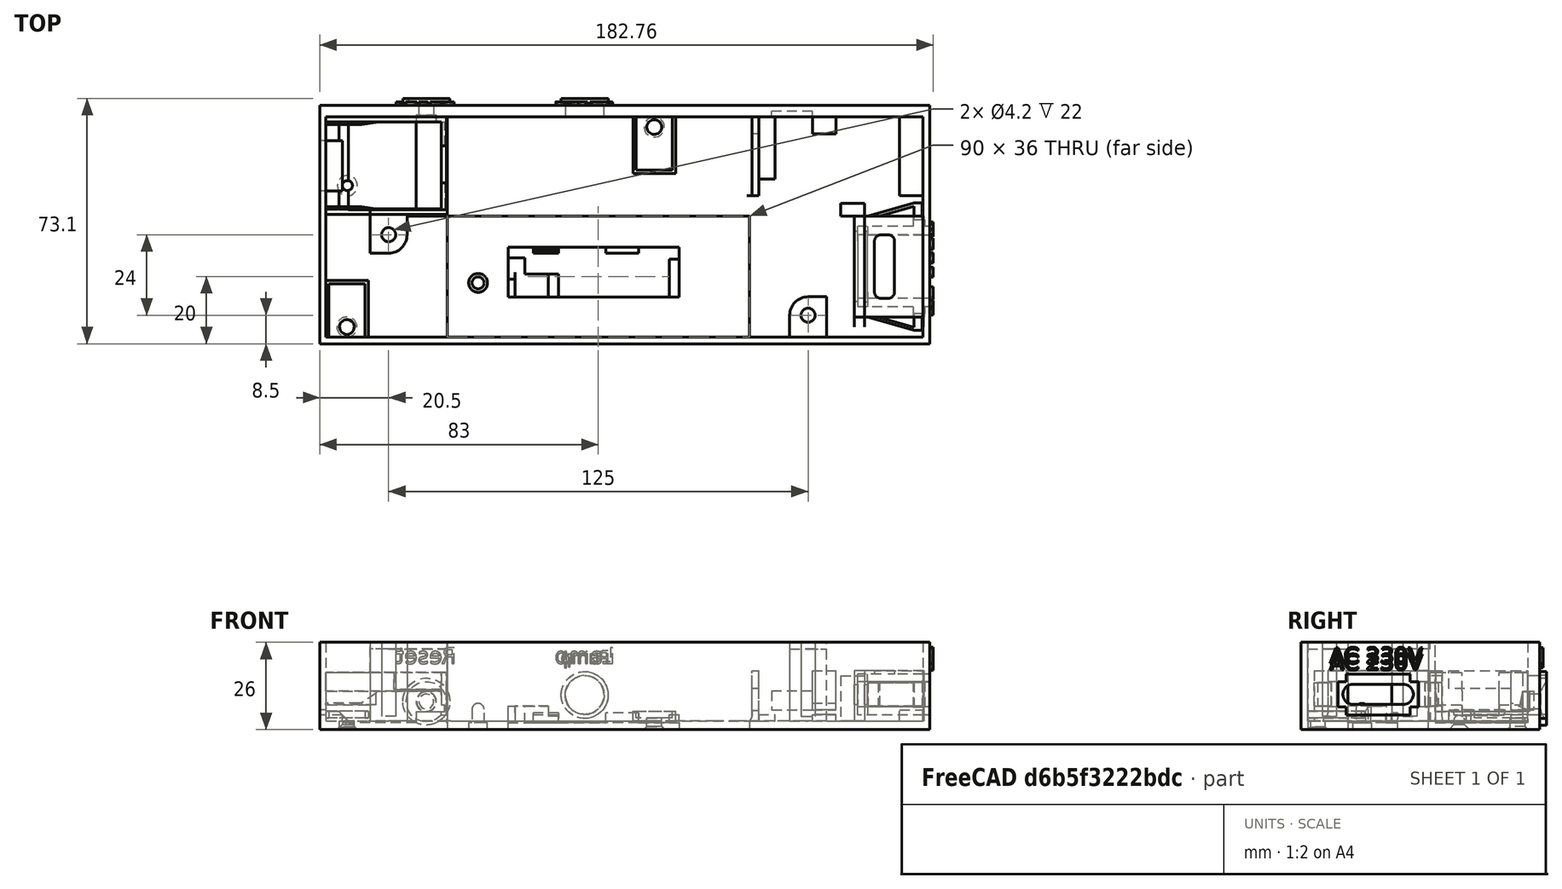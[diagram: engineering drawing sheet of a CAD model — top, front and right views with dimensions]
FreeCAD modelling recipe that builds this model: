
FCSTD DOCUMENT  (FreeCAD 0.21R33771 (Git))
Label: station.lamp.1x42V
License: All rights reserved
LicenseURL: http://en.wikipedia.org/wiki/All_rights_reserved
objects: Part::FeaturePython×10, Part::Extrusion×8, Part::Cut×6, Part::Feature×6, Part::MultiFuse×6, Part::Part2DObjectPython×6, App::DocumentObjectGroup×2, Part::Cone×1, Part::Refine×1
note: 44 computed .brp shape members not serialized (recipe doc carries the construction recipe); baked Part::Feature solids carry a one-line shape summary decoded from their .brp

FEATURE [Part::Cut] Cut008
FEATURE [Part::Feature] Cut008_solid  label="Cut008 (Solid)"
  shape: bbox 182.8 x 74.77 x 26 mm, 631 faces (baked)
FEATURE [Part::Feature] Fusion005002002014004003003002009002010004002003006003008008004007002004008002005001  label="Fusion005002002014004003003002009002010004002003006003008008004007002004008002006"
  Placement = pos=(-44.5951,-46.9627,187.501) rot=(0,0,1;1.5708rad)
  shape: bbox 50.9 x 14.8 x 7 mm, 30 faces (baked)
FEATURE [Part::MultiFuse] Fusion005002002014004003003002009002010004002003006003008008004007002004008002003
  Placement = pos=(333.004,-68.3059,2.13395) rot=(0,0,1;0rad)
FEATURE [Part::Part2DObjectPython] Rectangle  # Draft 2D object (typed FeaturePython)
  Area = 4964
  ChamferSize = 0
  Columns = 1
  FilletRadius = 0
  Height = 136
  Length = 36.5
  MakeFace = true
  Placement = pos=(136,3,22) rot=(0,0,1;1.5708rad)
  Rows = 1
FEATURE [Part::Extrusion] Extrusion
  Base = -> Rectangle
  Dir = (-8.1519e-11,-1.28811e-08,-2)
  DirMode = 0
  FaceMakerClass = Part::FaceMakerBullseye
  LengthFwd = 0
  LengthRev = 0
  Solid = true
  Symmetric = false
FEATURE [Part::Cut] Cut
  Base = -> Cut008_solid
  Tool = -> Extrusion
FEATURE [Part::Part2DObjectPython] Rectangle001  # Draft 2D object (typed FeaturePython)
  Area = 5003.74
  ChamferSize = 0
  Columns = 1
  FilletRadius = 0
  Height = 49.6839
  Length = 100.711
  MakeFace = true
  Placement = pos=(166.761,-20.8491,-24.6542) rot=(0.57735,0.57735,0.57735;2.0944rad)
  Rows = 1
FEATURE [Part::FeaturePython] Slice  # WARN: FeaturePython — macro-defined, semantics opaque (R4)
  Base = -> Cut
  Mode = 1
  Tolerance = 0
  Tools = -> [Rectangle001]
FEATURE [Part::FeaturePython] Slice_child0  label="Slice.0"  # WARN: FeaturePython — macro-defined, semantics opaque (R4)
  Base = -> Slice
  FilterType = 1
  Invert = false
  OverrideMaxVal = 0
  WindowFrom = 80
  WindowTo = 100
  items = 0
FEATURE [Part::FeaturePython] Slice_child1  label="Slice.1"  # WARN: FeaturePython — macro-defined, semantics opaque (R4)
  Base = -> Slice
  FilterType = 1
  Invert = false
  OverrideMaxVal = 0
  WindowFrom = 80
  WindowTo = 100
  items = 1
FEATURE [Part::FeaturePython] Slice_child2  label="Slice.2"  # WARN: FeaturePython — macro-defined, semantics opaque (R4)
  Base = -> Slice
  FilterType = 1
  Invert = false
  OverrideMaxVal = 0
  WindowFrom = 80
  WindowTo = 100
  items = 2
FEATURE [Part::FeaturePython] Slice_child3  label="Slice.3"  # WARN: FeaturePython — macro-defined, semantics opaque (R4)
  Base = -> Slice
  FilterType = 1
  Invert = false
  OverrideMaxVal = 0
  WindowFrom = 80
  WindowTo = 100
  items = 3
FEATURE [Part::FeaturePython] Slice_child4  label="Slice.4"  # WARN: FeaturePython — macro-defined, semantics opaque (R4)
  Base = -> Slice
  FilterType = 1
  Invert = false
  OverrideMaxVal = 0
  WindowFrom = 80
  WindowTo = 100
  items = 4
FEATURE [Part::FeaturePython] Slice_child5  label="Slice.5"  # WARN: FeaturePython — macro-defined, semantics opaque (R4)
  Base = -> Slice
  FilterType = 1
  Invert = false
  OverrideMaxVal = 0
  WindowFrom = 80
  WindowTo = 100
  items = 5
FEATURE [Part::FeaturePython] Slice_child6  label="Slice.6"  # WARN: FeaturePython — macro-defined, semantics opaque (R4)
  Base = -> Slice
  FilterType = 1
  Invert = false
  OverrideMaxVal = 0
  WindowFrom = 80
  WindowTo = 100
  items = 6
FEATURE [Part::MultiFuse] Fusion
  Placement = pos=(4.18709e-10,0,2) rot=(0,0,1;0rad)
  Shapes = -> [Slice_child6,Slice_child5,Slice_child4,Slice_child3,Slice_child2,Slice_child1]
FEATURE [Part::MultiFuse] Fusion005002002014004003003002009002010004002003006003008008004007002004008002005002
  Shapes = -> [Fusion,Slice_child0]
FEATURE [Part::Part2DObjectPython] Wire  # Draft 2D object (typed FeaturePython)
  Area = 5
  ChamferSize = 0
  Closed = true
  End = (131.761,63.6,1.9)
  FilletRadius = 0
  Length = 12.3852
  MakeFace = true
  Placement = pos=(131.761,68.6,1.9) rot=(-0.57735,0.57735,0.57735;4.18879rad)
  Points = (3) [(0,0,0),(5,2,-4.86691e-09),(5,-6.40528e-10,1.95172e-09)]
  Start = (131.761,68.6,1.9)
  Subdivisions = 0
FEATURE [Part::Extrusion] Extrusion001
  Base = -> Wire
  Dir = (7,-8.40441e-09,-2.13773e-08)
  DirMode = 0
  FaceMakerClass = Part::FaceMakerBullseye
  LengthFwd = 0
  LengthRev = 0
  Solid = true
  Symmetric = false
FEATURE [Part::Cut] Cut009
  Base = -> Fusion005002002014004003003002009002010004002003006003008008004007002004008002005002
  Tool = -> Extrusion001
FEATURE [Part::Feature] Face
  shape: bbox 0.0005987 x 24 x 12.2 mm, 1 faces, 0 solids (baked)
FEATURE [Part::Extrusion] Extrusion002
  Base = -> Face
  Dir = (-3,-3e-15,1.56777e-10)
  DirMode = 0
  FaceMakerClass = Part::FaceMakerBullseye
  LengthFwd = 0
  LengthRev = 0
  Solid = true
  Symmetric = false
FEATURE [Part::Cut] Cut010
  Base = -> Cut009
  Tool = -> Extrusion002
FEATURE [Part::Feature] Face001
  shape: bbox 0.0006002 x 33 x 15 mm, 1 faces, 0 solids (baked)
FEATURE [Part::Extrusion] Extrusion004
  Base = -> Face001
  Dir = (-2,1.46e-14,1.04524e-10)
  DirMode = 0
  FaceMakerClass = Part::FaceMakerBullseye
  LengthFwd = 0
  LengthRev = 0
  Solid = true
  Symmetric = false
FEATURE [Part::MultiFuse] Fusion005002002014004003003002009002010004002003006003008008004007002004008002005003
  Shapes = -> [Cut010,Extrusion004]
FEATURE [Part::Feature] Face002
  Placement = pos=(-12.2614,0.5,7.5) rot=(0,0,1;0rad)
  shape: bbox 0.0005987 x 24 x 12.2 mm, 1 faces, 0 solids (baked)
FEATURE [Part::Extrusion] Extrusion005
  Base = -> Face002
  Dir = (1,1e-15,-5.2259e-11)
  DirMode = 0
  FaceMakerClass = Part::FaceMakerBullseye
  LengthFwd = 0
  LengthRev = 0
  Placement = pos=(8.26138,-0.5,-7.5) rot=(0,0,1;0rad)
  Solid = true
  Symmetric = false
FEATURE [Part::Feature] Face003
  Placement = pos=(-2,1.5e-14,1.04524e-10) rot=(0,0,1;0rad)
  shape: bbox 0.0006002 x 33 x 15 mm, 1 faces, 0 solids (baked)
FEATURE [Part::Extrusion] Extrusion006
  Base = -> Face003
  Dir = (-1,7.3e-15,5.22618e-11)
  DirMode = 0
  FaceMakerClass = Part::FaceMakerBullseye
  LengthFwd = 0
  LengthRev = 0
  Solid = true
  Symmetric = false
FEATURE [Part::MultiFuse] Fusion005002002014004003003002009002010004002003006003008008004007002004008002005004
  Shapes = -> [Extrusion006,Extrusion005,Fusion005002002014004003003002009002010004002003006003008008004007002004008002005003]
FEATURE [Part::Cone] Cone
  Angle = 360
  AttacherType = Attacher::AttachEngine3D
  Height = 1.5
  Placement = pos=(-6.92,6,-4) rot=(0,0,1;0rad)
  Radius1 = 3
  Radius2 = 1.5
FEATURE [Part::Cut] Cut011
  Base = -> Fusion005002002014004003003002009002010004002003006003008008004007002004008002005004
  Tool = -> Cone
FEATURE [App::DocumentObjectGroup] GrExplode_Slice  label="Exploded Slice"
  Group = -> [Cut011]
FEATURE [Part::Refine] Cut012
  Source = -> Cut011
FEATURE [Part::Part2DObjectPython] Circle  # Draft 2D object (typed FeaturePython)
  Area = 28.2743
  FirstAngle = 0
  LastAngle = 0
  MakeFace = true
  Placement = pos=(16.73,67.1,4.33988) rot=(1,0,0;1.5708rad)
  Radius = 3
FEATURE [Part::Extrusion] Extrusion007
  Base = -> Circle
  Dir = (3.40484e-11,2,-4.42676e-09)
  DirMode = 0
  FaceMakerClass = Part::FaceMakerBullseye
  LengthFwd = 0
  LengthRev = 0
  Solid = true
  Symmetric = false
FEATURE [Part::Cut] Cut013
  Base = -> Cut012
  Tool = -> Extrusion007
FEATURE [Part::Part2DObjectPython] Rectangle002  # Draft 2D object (typed FeaturePython)
  Area = 1591.6
  ChamferSize = 0
  Columns = 1
  FilletRadius = 0
  Height = 39.6746
  Length = 40.1162
  MakeFace = true
  Placement = pos=(79.5251,72.1,13.7777) rot=(0,0.707107,0.707107;3.14159rad)
  Rows = 1
FEATURE [Part::FeaturePython] Slice001  # WARN: FeaturePython — macro-defined, semantics opaque (R4)
  Base = -> Cut013
  Mode = 1
  Tolerance = 0
  Tools = -> [Rectangle002]
FEATURE [Part::FeaturePython] Slice001_child0  label="Slice001.0"  # WARN: FeaturePython — macro-defined, semantics opaque (R4)
  Base = -> Slice001
  FilterType = 1
  Invert = false
  OverrideMaxVal = 0
  WindowFrom = 80
  WindowTo = 100
  items = 0
FEATURE [Part::Part2DObjectPython] ShapeString  # Draft 2D object (typed FeaturePython)
  FontFile = <path>
  MakeFace = true
  Placement = pos=(72.9009,72.1,15.7144) rot=(0,0.707107,0.707107;3.14159rad)
  Size = 5
  String = Lamp
  Tracking = 0
FEATURE [Part::Extrusion] Extrude
  Base = -> ShapeString
  Dir = (1.65013e-10,1,-2.23202e-09)
  DirMode = 2
  FaceMakerClass = Part::FaceMakerBullseye
  LengthFwd = 1
  LengthRev = 0
  Solid = false
  Symmetric = false
FEATURE [Part::MultiFuse] Fusion005002002014004003003002009002010004002003006003008008004007002004008002005005
  Shapes = -> [Slice001_child0,Extrude]
FEATURE [App::DocumentObjectGroup] GrExplode_Slice001  label="Exploded Slice001"
  Group = -> [Fusion005002002014004003003002009002010004002003006003008008004007002004008002005005]
note: 1 file-system path scrubbed to <path> (originals preserved in the JSON sidecar)
